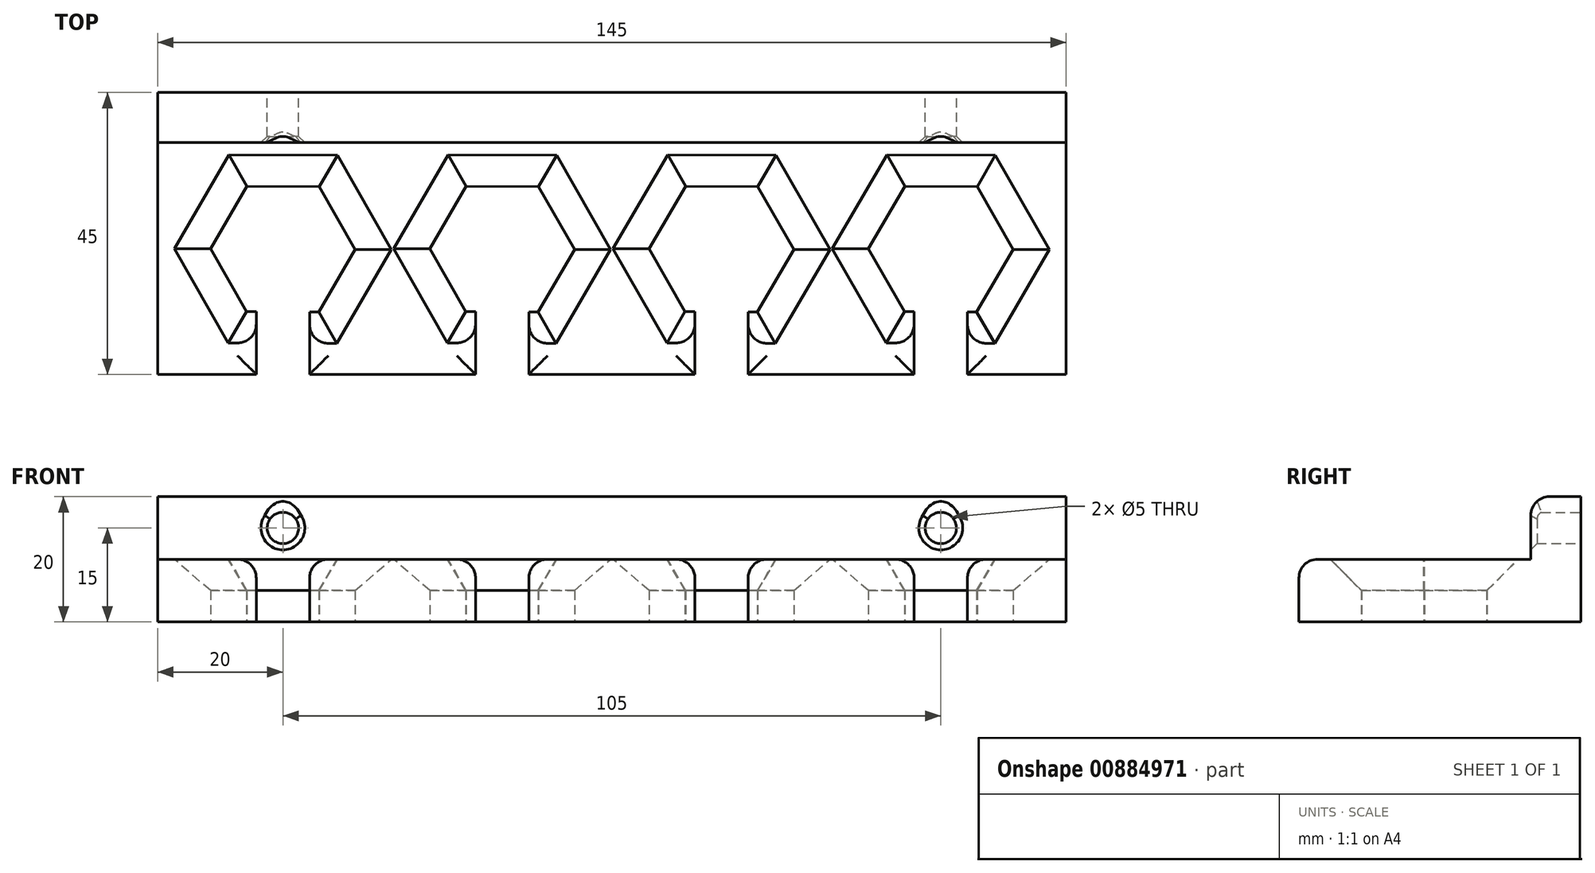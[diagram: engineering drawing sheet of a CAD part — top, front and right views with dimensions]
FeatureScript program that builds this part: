
annotation { "Feature Type Name" : "Feature", "Feature Type Description" : "" }
export const myFeature = defineFeature(function(context is Context, id is Id, definition is map)
    precondition{}
    {
        {
            var Q0;
            Q0=qCreatedBy(makeId("Top.planeOp"),FACE);
            var sketch = newSketch(context, id + "F0", { "sketchPlane" : qUnion([Q0])});
            skLineSegment(sketch, "E0", {"start": v(-95.3, -2.5) * mm, "end": v(98.27, -2.5) * mm, "construction": true});
            skLineSegment(sketch, "E1", {"start": v(-52.5, 32.5) * mm, "end": v(-52.5, -37.5) * mm, "construction": true});
            skCircle(sketch, "E2", {"center": v(-52.5, -37.5) * mm, "radius": 4.25 * mm});
            skLineSegment(sketch, "E3.bottom", {"start": v(-48.25, -37.5) * mm, "end": v(-56.75, -37.5) * mm});
            skLineSegment(sketch, "E3.top", {"start": v(-48.25, -2.5) * mm, "end": v(-56.75, -2.5) * mm});
            skLineSegment(sketch, "E3.left", {"start": v(-48.25, -37.5) * mm, "end": v(-48.25, -2.5) * mm});
            skLineSegment(sketch, "E3.right", {"start": v(-56.75, -37.5) * mm, "end": v(-56.75, -2.5) * mm});
            skLineSegment(sketch, "E4.bottom", {"start": v(-72.5, 22.5) * mm, "end": v(72.5, 22.5) * mm});
            skLineSegment(sketch, "E4.top", {"start": v(-72.5, -22.5) * mm, "end": v(72.5, -22.5) * mm});
            skLineSegment(sketch, "E4.left", {"start": v(-72.5, 22.5) * mm, "end": v(-72.5, -22.5) * mm});
            skLineSegment(sketch, "E4.right", {"start": v(72.5, 22.5) * mm, "end": v(72.5, -22.5) * mm});
            skLineSegment(sketch, "E5.0", {"start": v(-64.05, -2.45) * mm, "end": v(-58.23, 7.52) * mm});
            skLineSegment(sketch, "E5.1", {"start": v(-58.23, 7.52) * mm, "end": v(-46.69, 7.48) * mm});
            skLineSegment(sketch, "E5.2", {"start": v(-46.69, 7.48) * mm, "end": v(-40.95, -2.55) * mm});
            skLineSegment(sketch, "E5.3", {"start": v(-40.95, -2.55) * mm, "end": v(-46.77, -12.52) * mm});
            skLineSegment(sketch, "E5.4", {"start": v(-46.77, -12.52) * mm, "end": v(-58.31, -12.48) * mm});
            skLineSegment(sketch, "E5.5", {"start": v(-58.31, -12.48) * mm, "end": v(-64.05, -2.45) * mm});
            skLineSegment(sketch, "E6.1.0.0", {"start": v(-11.69, 7.48) * mm, "end": v(-5.95, -2.55) * mm});
            skLineSegment(sketch, "E6.1.0.1", {"start": v(-13.25, -37.5) * mm, "end": v(-13.25, -2.5) * mm});
            skLineSegment(sketch, "E6.1.0.2", {"start": v(-23.23, 7.52) * mm, "end": v(-11.69, 7.48) * mm});
            skLineSegment(sketch, "E6.1.0.3", {"start": v(-23.31, -12.48) * mm, "end": v(-29.05, -2.45) * mm});
            skLineSegment(sketch, "E6.1.0.4", {"start": v(-21.75, -37.5) * mm, "end": v(-21.75, -2.5) * mm});
            skLineSegment(sketch, "E6.1.0.5", {"start": v(-29.05, -2.45) * mm, "end": v(-23.23, 7.52) * mm});
            skCircle(sketch, "E6.1.0.6", {"center": v(-17.5, -37.5) * mm, "radius": 4.25 * mm});
            skLineSegment(sketch, "E6.1.0.7", {"start": v(-11.77, -12.52) * mm, "end": v(-23.31, -12.48) * mm});
            skLineSegment(sketch, "E6.1.0.8", {"start": v(-17.5, 32.5) * mm, "end": v(-17.5, -37.5) * mm, "construction": true});
            skLineSegment(sketch, "E6.1.0.9", {"start": v(-5.95, -2.55) * mm, "end": v(-11.77, -12.52) * mm});
            skLineSegment(sketch, "E6.1.0.10", {"start": v(-13.25, -2.5) * mm, "end": v(-21.75, -2.5) * mm});
            skLineSegment(sketch, "E6.1.0.11", {"start": v(-13.25, -37.5) * mm, "end": v(-21.75, -37.5) * mm});
            skLineSegment(sketch, "E6.2.0.0", {"start": v(23.31, 7.48) * mm, "end": v(29.05, -2.55) * mm});
            skLineSegment(sketch, "E6.2.0.1", {"start": v(21.75, -37.5) * mm, "end": v(21.75, -2.5) * mm});
            skLineSegment(sketch, "E6.2.0.2", {"start": v(11.77, 7.52) * mm, "end": v(23.31, 7.48) * mm});
            skLineSegment(sketch, "E6.2.0.3", {"start": v(11.69, -12.48) * mm, "end": v(5.95, -2.45) * mm});
            skLineSegment(sketch, "E6.2.0.4", {"start": v(13.25, -37.5) * mm, "end": v(13.25, -2.5) * mm});
            skLineSegment(sketch, "E6.2.0.5", {"start": v(5.95, -2.45) * mm, "end": v(11.77, 7.52) * mm});
            skCircle(sketch, "E6.2.0.6", {"center": v(17.5, -37.5) * mm, "radius": 4.25 * mm});
            skLineSegment(sketch, "E6.2.0.7", {"start": v(23.23, -12.52) * mm, "end": v(11.69, -12.48) * mm});
            skLineSegment(sketch, "E6.2.0.8", {"start": v(17.5, 32.5) * mm, "end": v(17.5, -37.5) * mm, "construction": true});
            skLineSegment(sketch, "E6.2.0.9", {"start": v(29.05, -2.55) * mm, "end": v(23.23, -12.52) * mm});
            skLineSegment(sketch, "E6.2.0.10", {"start": v(21.75, -2.5) * mm, "end": v(13.25, -2.5) * mm});
            skLineSegment(sketch, "E6.2.0.11", {"start": v(21.75, -37.5) * mm, "end": v(13.25, -37.5) * mm});
            skLineSegment(sketch, "E6.3.0.0", {"start": v(58.31, 7.48) * mm, "end": v(64.05, -2.55) * mm});
            skLineSegment(sketch, "E6.3.0.1", {"start": v(56.75, -37.5) * mm, "end": v(56.75, -2.5) * mm});
            skLineSegment(sketch, "E6.3.0.2", {"start": v(46.77, 7.52) * mm, "end": v(58.31, 7.48) * mm});
            skLineSegment(sketch, "E6.3.0.3", {"start": v(46.69, -12.48) * mm, "end": v(40.95, -2.45) * mm});
            skLineSegment(sketch, "E6.3.0.4", {"start": v(48.25, -37.5) * mm, "end": v(48.25, -2.5) * mm});
            skLineSegment(sketch, "E6.3.0.5", {"start": v(40.95, -2.45) * mm, "end": v(46.77, 7.52) * mm});
            skCircle(sketch, "E6.3.0.6", {"center": v(52.5, -37.5) * mm, "radius": 4.25 * mm});
            skLineSegment(sketch, "E6.3.0.7", {"start": v(58.23, -12.52) * mm, "end": v(46.69, -12.48) * mm});
            skLineSegment(sketch, "E6.3.0.8", {"start": v(52.5, 32.5) * mm, "end": v(52.5, -37.5) * mm, "construction": true});
            skLineSegment(sketch, "E6.3.0.9", {"start": v(64.05, -2.55) * mm, "end": v(58.23, -12.52) * mm});
            skLineSegment(sketch, "E6.3.0.10", {"start": v(56.75, -2.5) * mm, "end": v(48.25, -2.5) * mm});
            skLineSegment(sketch, "E6.3.0.11", {"start": v(56.75, -37.5) * mm, "end": v(48.25, -37.5) * mm});
            skLineSegment(sketch, "E6.direction1", {"start": v(-56.75, -37.5) * mm, "end": v(-21.75, -37.5) * mm, "construction": true});
            skSolve(sketch);
        }
        {
            var Q0;
            Q0=makeQuery(id+"F0.imprint","IMPRINT",FACE,{"disambiguationData":[TD([[makeQuery(id+"F0.imprint","IMPRINT",EDGE,{"derivedFrom":sQuery(id+"F0.wireOp",EDGE,"E4.bottom")}),-1.0]])]});
            extrude(context, id + "F1", {"entities" : qUnion([Q0]), "depth" : 10 * mm, "offsetDistance" : 25 * mm});
        }
        {
            var Q0;
            Q0=makeQuery(id+"F1.opExtrude","CAP_EDGE",EDGE,{"disambiguationData":[OSD([sQuery(id+"F0.wireOp",EDGE,"E5.5")])],"isStart":false});
            var Q1;
            Q1=makeQuery(id+"F1.opExtrude","CAP_EDGE",EDGE,{"disambiguationData":[OSD([sQuery(id+"F0.wireOp",EDGE,"E5.0")])],"isStart":false});
            var Q2;
            Q2=makeQuery(id+"F1.opExtrude","CAP_EDGE",EDGE,{"disambiguationData":[OSD([sQuery(id+"F0.wireOp",EDGE,"E5.1")])],"isStart":false});
            var Q3;
            Q3=makeQuery(id+"F1.opExtrude","CAP_EDGE",EDGE,{"disambiguationData":[OSD([sQuery(id+"F0.wireOp",EDGE,"E5.2")])],"isStart":false});
            var Q4;
            Q4=makeQuery(id+"F1.opExtrude","CAP_EDGE",EDGE,{"disambiguationData":[OSD([sQuery(id+"F0.wireOp",EDGE,"E5.3")])],"isStart":false});
            var Q5;
            {var subQ0=sQuery(id+"F0.wireOp",EDGE,"E5.4");Q5=makeQuery(id+"F1.opExtrude","CAP_EDGE",EDGE,{"disambiguationData":[OSD([subQ0]),TDD([makeQuery(id+"F0.imprint","IMPRINT",EDGE,{"disambiguationData":[TD([[makeQuery(id+"F0.imprint","INTERSECT",VERTEX,{"derivedFrom":[subQ0,sQuery(id+"F0.wireOp",EDGE,"E5.5")]}),1.0]])],"derivedFrom":subQ0})])],"isStart":false});}
            var Q6;
            {var subQ0=sQuery(id+"F0.wireOp",EDGE,"E5.4");Q6=makeQuery(id+"F1.opExtrude","CAP_EDGE",EDGE,{"disambiguationData":[OSD([subQ0]),TDD([makeQuery(id+"F0.imprint","IMPRINT",EDGE,{"disambiguationData":[TD([[makeQuery(id+"F0.imprint","INTERSECT",VERTEX,{"derivedFrom":[sQuery(id+"F0.wireOp",EDGE,"E5.3"),subQ0]}),-1.0]])],"derivedFrom":subQ0})])],"isStart":false});}
            var Q7;
            Q7=makeQuery(id+"F1.opExtrude","CAP_EDGE",EDGE,{"disambiguationData":[OSD([sQuery(id+"F0.wireOp",EDGE,"E6.1.0.5")])],"isStart":false});
            var Q8;
            Q8=makeQuery(id+"F1.opExtrude","CAP_EDGE",EDGE,{"disambiguationData":[OSD([sQuery(id+"F0.wireOp",EDGE,"E6.1.0.2")])],"isStart":false});
            var Q9;
            Q9=makeQuery(id+"F1.opExtrude","CAP_EDGE",EDGE,{"disambiguationData":[OSD([sQuery(id+"F0.wireOp",EDGE,"E6.1.0.0")])],"isStart":false});
            var Q10;
            Q10=makeQuery(id+"F1.opExtrude","CAP_EDGE",EDGE,{"disambiguationData":[OSD([sQuery(id+"F0.wireOp",EDGE,"E6.1.0.9")])],"isStart":false});
            var Q11;
            Q11=makeQuery(id+"F1.opExtrude","CAP_EDGE",EDGE,{"disambiguationData":[OSD([sQuery(id+"F0.wireOp",EDGE,"E6.1.0.3")])],"isStart":false});
            var Q12;
            {var subQ0=sQuery(id+"F0.wireOp",EDGE,"E6.1.0.7");Q12=makeQuery(id+"F1.opExtrude","CAP_EDGE",EDGE,{"disambiguationData":[OSD([subQ0]),TDD([makeQuery(id+"F0.imprint","IMPRINT",EDGE,{"disambiguationData":[TD([[makeQuery(id+"F0.imprint","INTERSECT",VERTEX,{"derivedFrom":[sQuery(id+"F0.wireOp",EDGE,"E6.1.0.3"),subQ0]}),1.0]])],"derivedFrom":subQ0})])],"isStart":false});}
            var Q13;
            {var subQ0=sQuery(id+"F0.wireOp",EDGE,"E6.1.0.7");Q13=makeQuery(id+"F1.opExtrude","CAP_EDGE",EDGE,{"disambiguationData":[OSD([subQ0]),TDD([makeQuery(id+"F0.imprint","IMPRINT",EDGE,{"disambiguationData":[TD([[makeQuery(id+"F0.imprint","INTERSECT",VERTEX,{"derivedFrom":[subQ0,sQuery(id+"F0.wireOp",EDGE,"E6.1.0.9")]}),-1.0]])],"derivedFrom":subQ0})])],"isStart":false});}
            var Q14;
            Q14=makeQuery(id+"F1.opExtrude","CAP_EDGE",EDGE,{"disambiguationData":[OSD([sQuery(id+"F0.wireOp",EDGE,"E6.2.0.2")])],"isStart":false});
            var Q15;
            Q15=makeQuery(id+"F1.opExtrude","CAP_EDGE",EDGE,{"disambiguationData":[OSD([sQuery(id+"F0.wireOp",EDGE,"E6.2.0.5")])],"isStart":false});
            var Q16;
            Q16=makeQuery(id+"F1.opExtrude","CAP_EDGE",EDGE,{"disambiguationData":[OSD([sQuery(id+"F0.wireOp",EDGE,"E6.2.0.3")])],"isStart":false});
            var Q17;
            {var subQ0=sQuery(id+"F0.wireOp",EDGE,"E6.2.0.7");Q17=makeQuery(id+"F1.opExtrude","CAP_EDGE",EDGE,{"disambiguationData":[OSD([subQ0]),TDD([makeQuery(id+"F0.imprint","IMPRINT",EDGE,{"disambiguationData":[TD([[makeQuery(id+"F0.imprint","INTERSECT",VERTEX,{"derivedFrom":[sQuery(id+"F0.wireOp",EDGE,"E6.2.0.3"),subQ0]}),1.0]])],"derivedFrom":subQ0})])],"isStart":false});}
            var Q18;
            {var subQ0=sQuery(id+"F0.wireOp",EDGE,"E6.2.0.7");Q18=makeQuery(id+"F1.opExtrude","CAP_EDGE",EDGE,{"disambiguationData":[OSD([subQ0]),TDD([makeQuery(id+"F0.imprint","IMPRINT",EDGE,{"disambiguationData":[TD([[makeQuery(id+"F0.imprint","INTERSECT",VERTEX,{"derivedFrom":[subQ0,sQuery(id+"F0.wireOp",EDGE,"E6.2.0.9")]}),-1.0]])],"derivedFrom":subQ0})])],"isStart":false});}
            var Q19;
            Q19=makeQuery(id+"F1.opExtrude","CAP_EDGE",EDGE,{"disambiguationData":[OSD([sQuery(id+"F0.wireOp",EDGE,"E6.2.0.9")])],"isStart":false});
            var Q20;
            Q20=makeQuery(id+"F1.opExtrude","CAP_EDGE",EDGE,{"disambiguationData":[OSD([sQuery(id+"F0.wireOp",EDGE,"E6.2.0.0")])],"isStart":false});
            var Q21;
            Q21=makeQuery(id+"F1.opExtrude","CAP_EDGE",EDGE,{"disambiguationData":[OSD([sQuery(id+"F0.wireOp",EDGE,"E6.3.0.5")])],"isStart":false});
            var Q22;
            Q22=makeQuery(id+"F1.opExtrude","CAP_EDGE",EDGE,{"disambiguationData":[OSD([sQuery(id+"F0.wireOp",EDGE,"E6.3.0.2")])],"isStart":false});
            var Q23;
            Q23=makeQuery(id+"F1.opExtrude","CAP_EDGE",EDGE,{"disambiguationData":[OSD([sQuery(id+"F0.wireOp",EDGE,"E6.3.0.0")])],"isStart":false});
            var Q24;
            Q24=makeQuery(id+"F1.opExtrude","CAP_EDGE",EDGE,{"disambiguationData":[OSD([sQuery(id+"F0.wireOp",EDGE,"E6.3.0.9")])],"isStart":false});
            var Q25;
            {var subQ0=sQuery(id+"F0.wireOp",EDGE,"E6.3.0.7");Q25=makeQuery(id+"F1.opExtrude","CAP_EDGE",EDGE,{"disambiguationData":[OSD([subQ0]),TDD([makeQuery(id+"F0.imprint","IMPRINT",EDGE,{"disambiguationData":[TD([[makeQuery(id+"F0.imprint","INTERSECT",VERTEX,{"derivedFrom":[subQ0,sQuery(id+"F0.wireOp",EDGE,"E6.3.0.9")]}),-1.0]])],"derivedFrom":subQ0})])],"isStart":false});}
            var Q26;
            {var subQ0=sQuery(id+"F0.wireOp",EDGE,"E6.3.0.7");Q26=makeQuery(id+"F1.opExtrude","CAP_EDGE",EDGE,{"disambiguationData":[OSD([subQ0]),TDD([makeQuery(id+"F0.imprint","IMPRINT",EDGE,{"disambiguationData":[TD([[makeQuery(id+"F0.imprint","INTERSECT",VERTEX,{"derivedFrom":[sQuery(id+"F0.wireOp",EDGE,"E6.3.0.3"),subQ0]}),1.0]])],"derivedFrom":subQ0})])],"isStart":false});}
            var Q27;
            Q27=makeQuery(id+"F1.opExtrude","CAP_EDGE",EDGE,{"disambiguationData":[OSD([sQuery(id+"F0.wireOp",EDGE,"E6.3.0.3")])],"isStart":false});
            chamfer(context, id + "F2", {"entities" : qUnion([Q0, Q1, Q2, Q3, Q4, Q5, Q6, Q7, Q8, Q9, Q10, Q11, Q12, Q13, Q14, Q15, Q16, Q17, Q18, Q19, Q20, Q21, Q22, Q23, Q24, Q25, Q26, Q27]), "width" : 5 * mm, "tangentPropagation" : true});
        }
        {
            var Q0;
            Q0=makeQuery(id+"F1.opExtrude","CAP_FACE",FACE,{"disambiguationData":[OSD([sQuery(id+"F0.wireOp",EDGE,"2SCS3ArD-7dqZ-Jvp9-Svos-BSLdXjk2iGnL"),sQuery(id+"F0.wireOp",EDGE,"E3.left"),sQuery(id+"F0.wireOp",EDGE,"E3.right"),sQuery(id+"F0.wireOp",EDGE,"35d67615-0949-4875-a7f7-77961af0ef97.1.0.1"),sQuery(id+"F0.wireOp",EDGE,"35d67615-0949-4875-a7f7-77961af0ef97.1.0.2"),sQuery(id+"F0.wireOp",EDGE,"35d67615-0949-4875-a7f7-77961af0ef97.1.0.4"),sQuery(id+"F0.wireOp",EDGE,"35d67615-0949-4875-a7f7-77961af0ef97.2.0.1"),sQuery(id+"F0.wireOp",EDGE,"35d67615-0949-4875-a7f7-77961af0ef97.2.0.2"),sQuery(id+"F0.wireOp",EDGE,"35d67615-0949-4875-a7f7-77961af0ef97.2.0.4"),sQuery(id+"F0.wireOp",EDGE,"35d67615-0949-4875-a7f7-77961af0ef97.3.0.1"),sQuery(id+"F0.wireOp",EDGE,"35d67615-0949-4875-a7f7-77961af0ef97.3.0.2"),sQuery(id+"F0.wireOp",EDGE,"35d67615-0949-4875-a7f7-77961af0ef97.3.0.4"),sQuery(id+"F0.wireOp",EDGE,"E4.bottom"),sQuery(id+"F0.wireOp",EDGE,"E4.top"),sQuery(id+"F0.wireOp",EDGE,"E4.left"),sQuery(id+"F0.wireOp",EDGE,"E4.right")])],"isStart":false});
            var sketch = newSketch(context, id + "F3", { "sketchPlane" : qUnion([Q0])});
            skLineSegment(sketch, "E7.bottom", {"start": v(72.5, 22.5) * mm, "end": v(-72.5, 22.5) * mm});
            skLineSegment(sketch, "E7.top", {"start": v(72.5, 14.5) * mm, "end": v(-72.5, 14.5) * mm});
            skLineSegment(sketch, "E7.left", {"start": v(72.5, 22.5) * mm, "end": v(72.5, 14.5) * mm});
            skLineSegment(sketch, "E7.right", {"start": v(-72.5, 22.5) * mm, "end": v(-72.5, 14.5) * mm});
            skSolve(sketch);
        }
        {
            var Q0;
            Q0 = qSketchRegion(id + "F3", true);
            extrude(context, id + "F4", {"entities" : qUnion([Q0]), "operationType" : NewBodyOperationType.ADD, "depth" : 10 * mm, "offsetDistance" : 25 * mm});
        }
        {
            var Q0;
            Q0=makeQuery(id+"F1.opExtrude","CAP_EDGE",EDGE,{"disambiguationData":[OSD([sQuery(id+"F0.wireOp",EDGE,"E3.left")])],"isStart":false});
            var Q1;
            Q1=makeQuery(id+"F1.opExtrude","CAP_EDGE",EDGE,{"disambiguationData":[OSD([sQuery(id+"F0.wireOp",EDGE,"E3.right")])],"isStart":false});
            var Q2;
            {var subQ0=sQuery(id+"F0.wireOp",EDGE,"E4.top");Q2=makeQuery(id+"F1.opExtrude","CAP_EDGE",EDGE,{"disambiguationData":[OSD([subQ0]),TDD([makeQuery(id+"F0.imprint","IMPRINT",EDGE,{"disambiguationData":[TD([[makeQuery(id+"F0.imprint","INTERSECT",VERTEX,{"derivedFrom":[subQ0,sQuery(id+"F0.wireOp",EDGE,"E4.left")]}),-1.0]])],"derivedFrom":subQ0})])],"isStart":false});}
            var Q3;
            {var subQ0=sQuery(id+"F0.wireOp",EDGE,"E4.top");Q3=makeQuery(id+"F1.opExtrude","CAP_EDGE",EDGE,{"disambiguationData":[OSD([subQ0]),TDD([makeQuery(id+"F0.imprint","IMPRINT",EDGE,{"disambiguationData":[TD([[makeQuery(id+"F0.imprint","INTERSECT",VERTEX,{"derivedFrom":[sQuery(id+"F0.wireOp",EDGE,"E3.left"),subQ0]}),-1.0]])],"derivedFrom":subQ0})])],"isStart":false});}
            var Q4;
            Q4=makeQuery(id+"F1.opExtrude","CAP_EDGE",EDGE,{"disambiguationData":[OSD([sQuery(id+"F0.wireOp",EDGE,"E6.1.0.4")])],"isStart":false});
            var Q5;
            Q5=makeQuery(id+"F1.opExtrude","CAP_EDGE",EDGE,{"disambiguationData":[OSD([sQuery(id+"F0.wireOp",EDGE,"E6.1.0.1")])],"isStart":false});
            var Q6;
            {var subQ0=sQuery(id+"F0.wireOp",EDGE,"E4.top");Q6=makeQuery(id+"F1.opExtrude","CAP_EDGE",EDGE,{"disambiguationData":[OSD([subQ0]),TDD([makeQuery(id+"F0.imprint","IMPRINT",EDGE,{"disambiguationData":[TD([[makeQuery(id+"F0.imprint","INTERSECT",VERTEX,{"derivedFrom":[subQ0,sQuery(id+"F0.wireOp",EDGE,"E6.1.0.1")]}),-1.0]])],"derivedFrom":subQ0})])],"isStart":false});}
            var Q7;
            Q7=makeQuery(id+"F1.opExtrude","CAP_EDGE",EDGE,{"disambiguationData":[OSD([sQuery(id+"F0.wireOp",EDGE,"E6.2.0.4")])],"isStart":false});
            var Q8;
            Q8=makeQuery(id+"F1.opExtrude","CAP_EDGE",EDGE,{"disambiguationData":[OSD([sQuery(id+"F0.wireOp",EDGE,"E6.2.0.1")])],"isStart":false});
            var Q9;
            {var subQ0=sQuery(id+"F0.wireOp",EDGE,"E4.top");Q9=makeQuery(id+"F1.opExtrude","CAP_EDGE",EDGE,{"disambiguationData":[OSD([subQ0]),TDD([makeQuery(id+"F0.imprint","IMPRINT",EDGE,{"disambiguationData":[TD([[makeQuery(id+"F0.imprint","INTERSECT",VERTEX,{"derivedFrom":[subQ0,sQuery(id+"F0.wireOp",EDGE,"E6.2.0.1")]}),-1.0]])],"derivedFrom":subQ0})])],"isStart":false});}
            var Q10;
            Q10=makeQuery(id+"F1.opExtrude","CAP_EDGE",EDGE,{"disambiguationData":[OSD([sQuery(id+"F0.wireOp",EDGE,"E6.3.0.4")])],"isStart":false});
            var Q11;
            Q11=makeQuery(id+"F1.opExtrude","CAP_EDGE",EDGE,{"disambiguationData":[OSD([sQuery(id+"F0.wireOp",EDGE,"E6.3.0.1")])],"isStart":false});
            var Q12;
            {var subQ0=sQuery(id+"F0.wireOp",EDGE,"E4.top");Q12=makeQuery(id+"F1.opExtrude","CAP_EDGE",EDGE,{"disambiguationData":[OSD([subQ0]),TDD([makeQuery(id+"F0.imprint","IMPRINT",EDGE,{"disambiguationData":[TD([[makeQuery(id+"F0.imprint","INTERSECT",VERTEX,{"derivedFrom":[subQ0,sQuery(id+"F0.wireOp",EDGE,"E4.right")]}),1.0]])],"derivedFrom":subQ0})])],"isStart":false});}
            var Q13;
            Q13=makeQuery(id+"F4.opExtrude","CAP_EDGE",EDGE,{"disambiguationData":[OSD([sQuery(id+"F3.wireOp",EDGE,"E7.top")])],"isStart":false});
            var Q14;
            Q14=makeQuery(id+"F4.opExtrude","CAP_EDGE",EDGE,{"disambiguationData":[OSD([sQuery(id+"F3.wireOp",EDGE,"E7.top")])],"isStart":true});
            fillet(context, id + "F5", {"entities" : qUnion([Q0, Q1, Q2, Q3, Q4, Q5, Q6, Q7, Q8, Q9, Q10, Q11, Q12, Q13, Q14]), "radius" : 3 * mm, "tangentPropagation" : true, "allowEdgeOverflow" : false});
        }
        {
            var Q0;
            Q0=makeQuery(id+"F4.boolean.opBoolean","MERGE",FACE,{"derivedFrom":[makeQuery(id+"F1.opExtrude","SWEPT_FACE",FACE,{"disambiguationData":[OSD([sQuery(id+"F0.wireOp",EDGE,"E4.bottom")])]}),makeQuery(id+"F4.opExtrude","SWEPT_FACE",FACE,{"disambiguationData":[OSD([sQuery(id+"F3.wireOp",EDGE,"E7.bottom")])]})]});
            var sketch = newSketch(context, id + "F6", { "sketchPlane" : qUnion([Q0])});
            skLineSegment(sketch, "E8", {"start": v(-72.5, 15) * mm, "end": v(72.5, 15) * mm, "construction": true});
            skCircle(sketch, "E9", {"center": v(-52.5, 15) * mm, "radius": 2.5 * mm});
            skCircle(sketch, "E10", {"center": v(52.5, 15) * mm, "radius": 2.5 * mm});
            skSolve(sketch);
        }
        {
            var Q0;
            Q0 = qSketchRegion(id + "F6", true);
            extrude(context, id + "F7", {"entities" : qUnion([Q0]), "operationType" : NewBodyOperationType.REMOVE, "endBound" : BoundingType.THROUGH_ALL, "oppositeDirection" : true, "depth" : 25 * mm, "offsetDistance" : 25 * mm});
        }
        {
            var Q0;
            Q0=makeQuery(id+"F7.boolean.opBoolean","INTERSECT",EDGE,{"disambiguationData":[OD(1.0)],"derivedFrom":[makeQuery(id+"F4.opExtrude","SWEPT_FACE",FACE,{"disambiguationData":[OSD([sQuery(id+"F3.wireOp",EDGE,"E7.top")])]}),makeQuery(id+"F7.opExtrude","SWEPT_FACE",FACE,{"disambiguationData":[OSD([sQuery(id+"F6.wireOp",EDGE,"E10")])]})]});
            var Q1;
            Q1=makeQuery(id+"F7.boolean.opBoolean","INTERSECT",EDGE,{"disambiguationData":[OD(1.0)],"derivedFrom":[makeQuery(id+"F4.opExtrude","SWEPT_FACE",FACE,{"disambiguationData":[OSD([sQuery(id+"F3.wireOp",EDGE,"E7.top")])]}),makeQuery(id+"F7.opExtrude","SWEPT_FACE",FACE,{"disambiguationData":[OSD([sQuery(id+"F6.wireOp",EDGE,"E9")])]})]});
            chamfer(context, id + "F8", {"entities" : qUnion([Q0, Q1]), "width" : 1 * mm, "tangentPropagation" : true});
        }
    });
